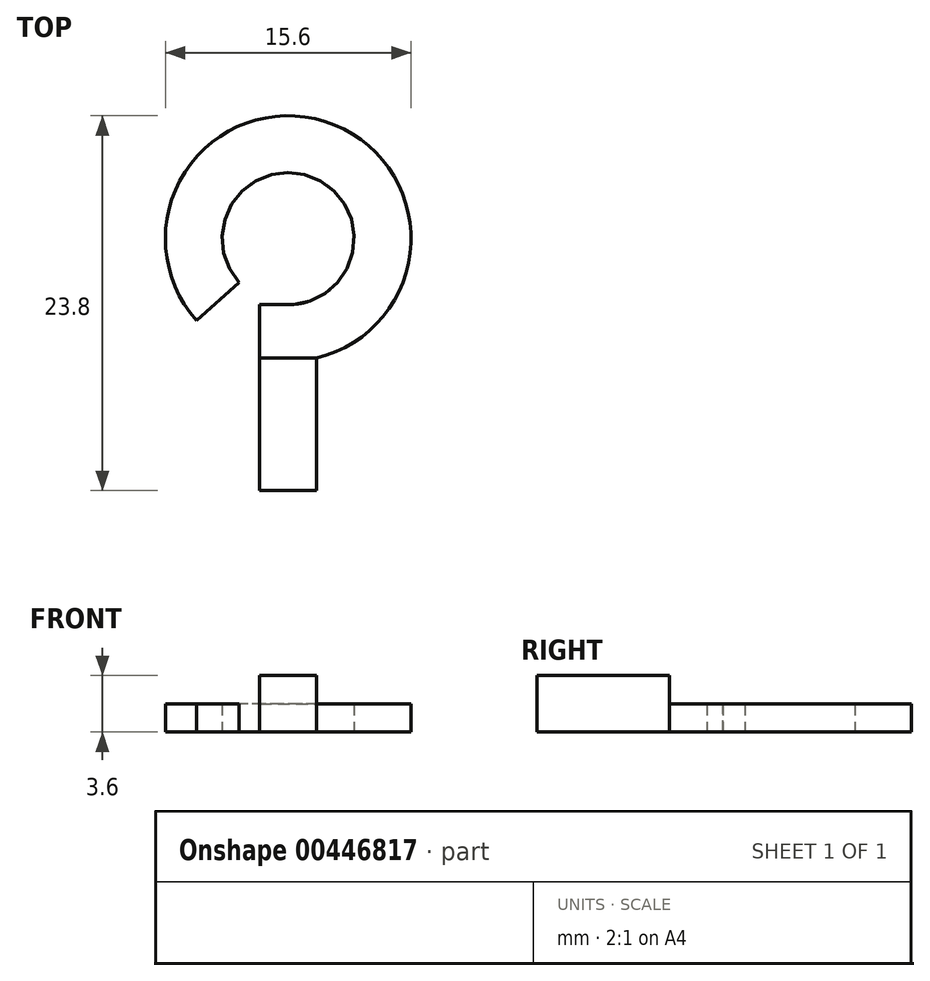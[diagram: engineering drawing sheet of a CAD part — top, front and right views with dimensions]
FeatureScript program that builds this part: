
annotation { "Feature Type Name" : "Feature", "Feature Type Description" : "" }
export const myFeature = defineFeature(function(context is Context, id is Id, definition is map)
    precondition{}
    {
        {
            var Q0;
            Q0=qCreatedBy(makeId("Top.planeOp"),FACE);
            var sketch = newSketch(context, id + "F0", { "sketchPlane" : qUnion([Q0])});
            skLineSegment(sketch, "E0", {"start": v(0, 0) * mm, "end": v(0, 10) * mm});
            skArc(sketch, "E1", {"start": v(0, 10) * mm, "mid": v(2.45, 21.48) * mm, "end": v(-4.47, 12) * mm});
            skSolve(sketch);
        }
        {
            var Q0;
            Q0=qCreatedBy(makeId("Front.planeOp"),FACE);
            var sketch = newSketch(context, id + "F1", { "sketchPlane" : qUnion([Q0])});
            skLineSegment(sketch, "E2.bottom", {"start": v(-1.8, 1.8) * mm, "end": v(1.8, 1.8) * mm});
            skLineSegment(sketch, "E2.top", {"start": v(-1.8, -1.8) * mm, "end": v(1.8, -1.8) * mm});
            skLineSegment(sketch, "E2.left", {"start": v(-1.8, 1.8) * mm, "end": v(-1.8, -1.8) * mm});
            skLineSegment(sketch, "E2.right", {"start": v(1.8, 1.8) * mm, "end": v(1.8, -1.8) * mm});
            skLineSegment(sketch, "E3", {"start": v(-1.8, -1.8) * mm, "end": v(1.8, 1.8) * mm, "construction": true});
            skPoint(sketch, "E4", {"position": v(0, 0) * mm});
            skSolve(sketch);
        }
        {
            var Q0;
            Q0=makeQuery(id+"F1.imprint","IMPRINT",FACE,{"disambiguationData":[TD([[makeQuery(id+"F1.imprint","IMPRINT",EDGE,{"derivedFrom":sQuery(id+"F1.wireOp",EDGE,"E2.bottom")}),-1.0]])]});
            var Q1;
            Q1=sQuery(id+"F0.wireOp",EDGE,"E0");
            var Q2;
            Q2=sQuery(id+"F0.wireOp",EDGE,"E1");
            sweep(context, id + "F2", {"profiles" : qUnion([Q0]), "path" : qUnion([Q1, Q2])});
        }
        {
            var Q0;
            Q0=qCreatedBy(makeId("Top.planeOp"),FACE);
            var sketch = newSketch(context, id + "F3", { "sketchPlane" : qUnion([Q0])});
            skLineSegment(sketch, "E5.bottom", {"start": v(-7.8, 8.41) * mm, "end": v(7.8, 8.41) * mm});
            skLineSegment(sketch, "E5.top", {"start": v(-7.8, 23.8) * mm, "end": v(7.8, 23.8) * mm});
            skLineSegment(sketch, "E5.left", {"start": v(-7.8, 8.41) * mm, "end": v(-7.8, 23.8) * mm});
            skLineSegment(sketch, "E5.right", {"start": v(7.8, 8.41) * mm, "end": v(7.8, 23.8) * mm});
            skPoint(sketch, "E6", {"position": v(0, 23.8) * mm});
            skLineSegment(sketch, "E7.0", {"start": v(1.8, 0) * mm, "end": v(1.8, 8.41) * mm, "construction": true});
            skPoint(sketch, "E8", {"position": v(1.8, 8.41) * mm});
            skSolve(sketch);
        }
        {
            var Q0;
            Q0 = qSketchRegion(id + "F3", true);
            extrude(context, id + "F4", {"entities" : qUnion([Q0]), "operationType" : NewBodyOperationType.REMOVE, "endBound" : BoundingType.THROUGH_ALL, "depth" : 25 * mm});
        }
    });
